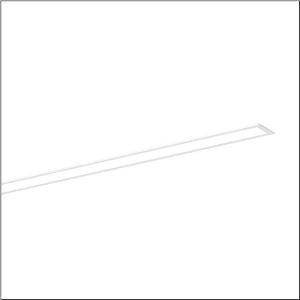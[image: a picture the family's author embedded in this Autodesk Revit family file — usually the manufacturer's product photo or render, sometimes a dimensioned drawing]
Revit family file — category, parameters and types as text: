
# Revit family: silica_r__21_51mx10db42wb_30ee
name_source: partatom
category: Lighting Fixtures
units: mm (PartAtom-declared; Revit-internal decimal feet)

## family parameters
Cut with Voids When Loaded = No
Host = Face
Light Source = No
Part Type = Normal
Room Calculation Point = No
Round Connector Dimension = Use Diameter
Shared = No

## types (1)
- --- (1 x LED, 3000 lm, 19 W, 4000K)
    Apparent Load = 19 VA
    CIE Flux Codes = 48 79 96 100 100
    Color Rendering = 80
    Color Temperature = 4000K
    Default Elevation = 1800 mm
    Description = Silica® 21, office luminaire, primary optical cover: cover, of PMMA, opal, light emission: direct distribution, primary light characteristic: symmetric, installation type: recessed, LED, rated luminous flux: 3.000lm, luminous efficacy: 158lm/W, light colour: 840, colour temperature: 4000K, with terminal, 3+2-pole, max. 2.5mm², mains connection: 220..240V, AC, 50/60Hz, rated input power: 19W, luminaire housing, of aluminium, traffic white (RAL 9016), length: 1.528mm, width: 79mm, height: 53mm, protection rating (complete): IP20, insulation class (complete): insulation class I (protective earthing), certification: CE, permissible operating ambient temperature: 0..+35°C, standard: EN 50419, packaging unit: 1 piece
    Height = 0 mm  [stored 0 ft]
    Lamp = 1 x LED
    Lamp Light Flux = 3000 lm
    Lamp Power = 19 W
    Lamp count = 1
    Length = 1527 mm
    Luminous efficacy = 158 lm/W
    Manufacturer = Siteco
    ModVariant = No
    Model = 51MX10DB42WB
    Mounting Place = Ceiling
    Mounting Type = Recessed
    Number of Poles = 1
    OnlyDefault = Yes
    Power Factor = 1
    Product Name = Silica® 21
    Product group = office luminaire | ceiling recessed
    ProductGroupID = 401
    Protection Class = Protection class I
    Protection Degree = IP 20
    RLX_Detail_Level = 1
    RLX_Emergency_Light_Flux = 0 lm
    RLX_Emergency_Type = 0
    RLX_Emergency_Type_DB = No
    RlxData = <blob elided: 21033 chars, md5=89d574b5>
    Socket = socket
    Standby Power = 0 W
    System Light Flux = 3000 lm
    System Power = 19 W
    Type Comments = factory setting: luminous flux: 100 % | dim-lin: 254 | 218 mA
    Type Image = l_1297737.jpg
    URL = http://relux.com
    VarID = @adj_047717
    Voltage = 0 V
    Weight = 0.00 kg
    Width = 79 mm

note: [stored X ft] marks values corroborated as IEEE doubles in the binary element streams (Revit-internal decimal feet)

## geometry (parser evidence)
native form markers: Blend x4, Sweep x10
no freeform markers — native parametric forms only
